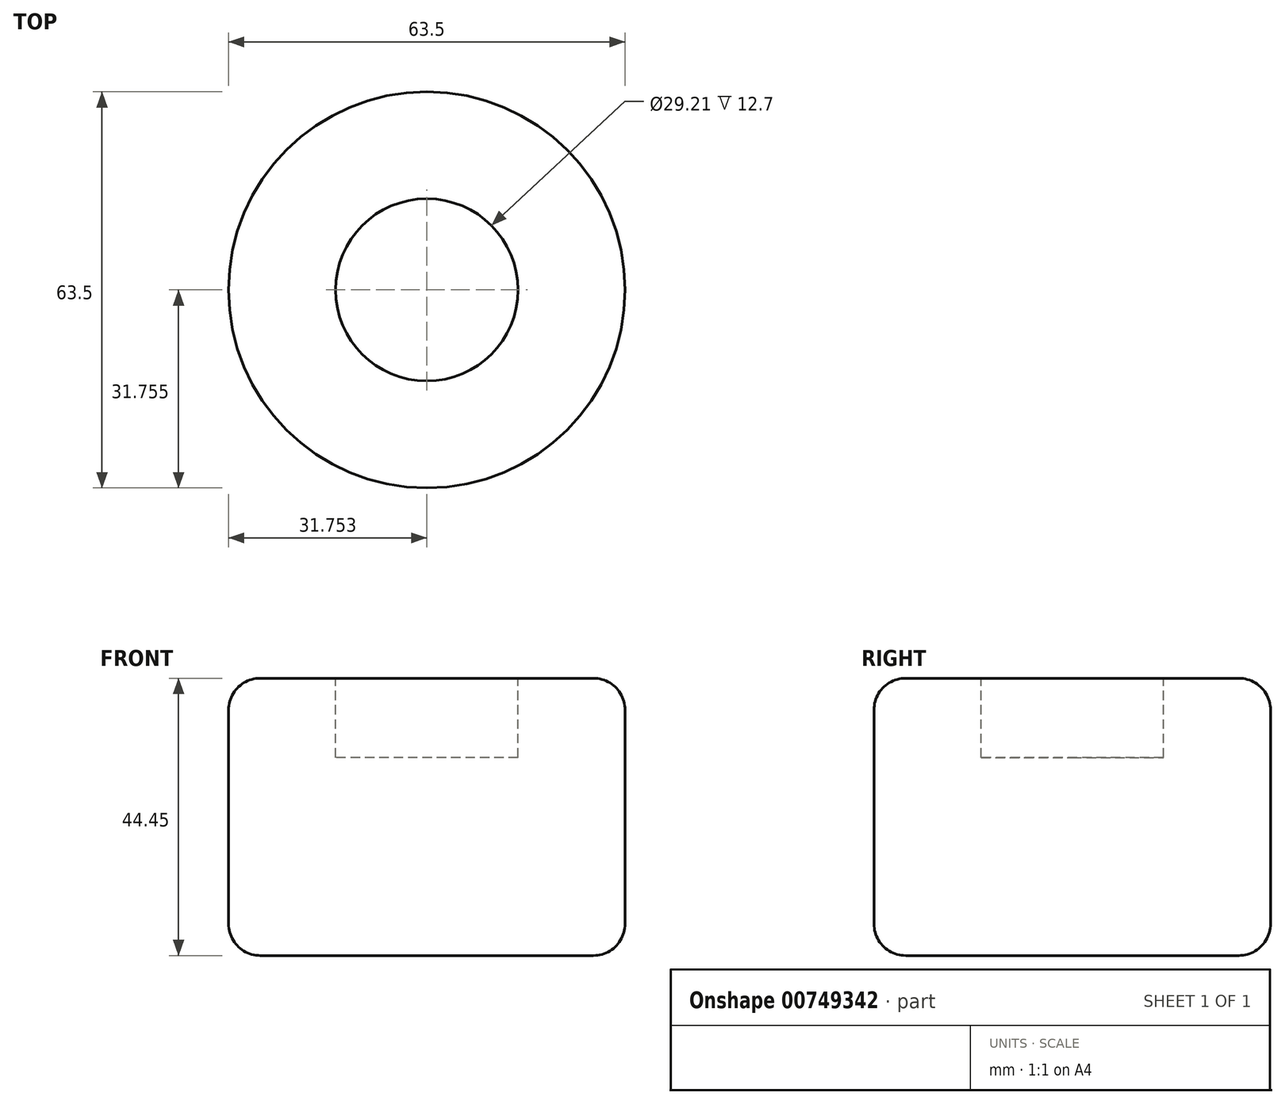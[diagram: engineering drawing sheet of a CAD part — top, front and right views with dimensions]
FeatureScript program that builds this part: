
annotation { "Feature Type Name" : "Feature", "Feature Type Description" : "" }
export const myFeature = defineFeature(function(context is Context, id is Id, definition is map)
    precondition{}
    {
        {
            var Q0;
            Q0=qCreatedBy(makeId("Top.planeOp"),FACE);
            var sketch = newSketch(context, id + "F0", { "sketchPlane" : qUnion([Q0])});
            skCircle(sketch, "E0", {"center": v(-17.24, 10.78) * mm, "radius": 31.75 * mm});
            skSolve(sketch);
        }
        {
            var Q0;
            Q0=makeQuery(id+"F0.imprint","IMPRINT",FACE,{"disambiguationData":[TD([[makeQuery(id+"F0.imprint","IMPRINT",EDGE,{"derivedFrom":sQuery(id+"F0.wireOp",EDGE,"E0")}),1.0]])]});
            extrude(context, id + "F1", {"entities" : qUnion([Q0]), "depth" : 44.45 * mm, "offsetDistance" : 25.4 * mm});
        }
        {
            var Q0;
            Q0=makeQuery(id+"F1.opExtrude","CAP_FACE",FACE,{"disambiguationData":[OSD([sQuery(id+"F0.wireOp",EDGE,"E0")])],"isStart":false});
            var sketch = newSketch(context, id + "F2", { "sketchPlane" : qUnion([Q0])});
            skCircle(sketch, "E1", {"center": v(-17.24, 10.78) * mm, "radius": 14.6 * mm});
            skSolve(sketch);
        }
        {
            var Q0;
            Q0=makeQuery(id+"F2.imprint","IMPRINT",FACE,{"disambiguationData":[TD([[makeQuery(id+"F2.imprint","IMPRINT",EDGE,{"derivedFrom":sQuery(id+"F2.wireOp",EDGE,"E1")}),1.0]])]});
            extrude(context, id + "F3", {"entities" : qUnion([Q0]), "operationType" : NewBodyOperationType.REMOVE, "oppositeDirection" : true, "depth" : 12.7 * mm, "offsetDistance" : 25.4 * mm});
        }
        {
            var Q0;
            Q0=makeQuery(id+"F1.opExtrude","CAP_EDGE",EDGE,{"disambiguationData":[OSD([sQuery(id+"F0.wireOp",EDGE,"E0")])],"isStart":false});
            var Q1;
            Q1=makeQuery(id+"F1.opExtrude","CAP_EDGE",EDGE,{"disambiguationData":[OSD([sQuery(id+"F0.wireOp",EDGE,"E0")])],"isStart":true});
            var Q2;
            Q2=makeQuery(id+"F3.boolean.opBoolean","COPY",EDGE,{"derivedFrom":makeQuery(id+"F3.opExtrude","CAP_EDGE",EDGE,{"disambiguationData":[OSD([sQuery(id+"F2.wireOp",EDGE,"E1")])],"isStart":true})});
            fillet(context, id + "F4", {"entities" : qUnion([Q0, Q1, Q2]), "radius" : 5.08 * mm, "tangentPropagation" : true, "allowEdgeOverflow" : false});
        }
    });
